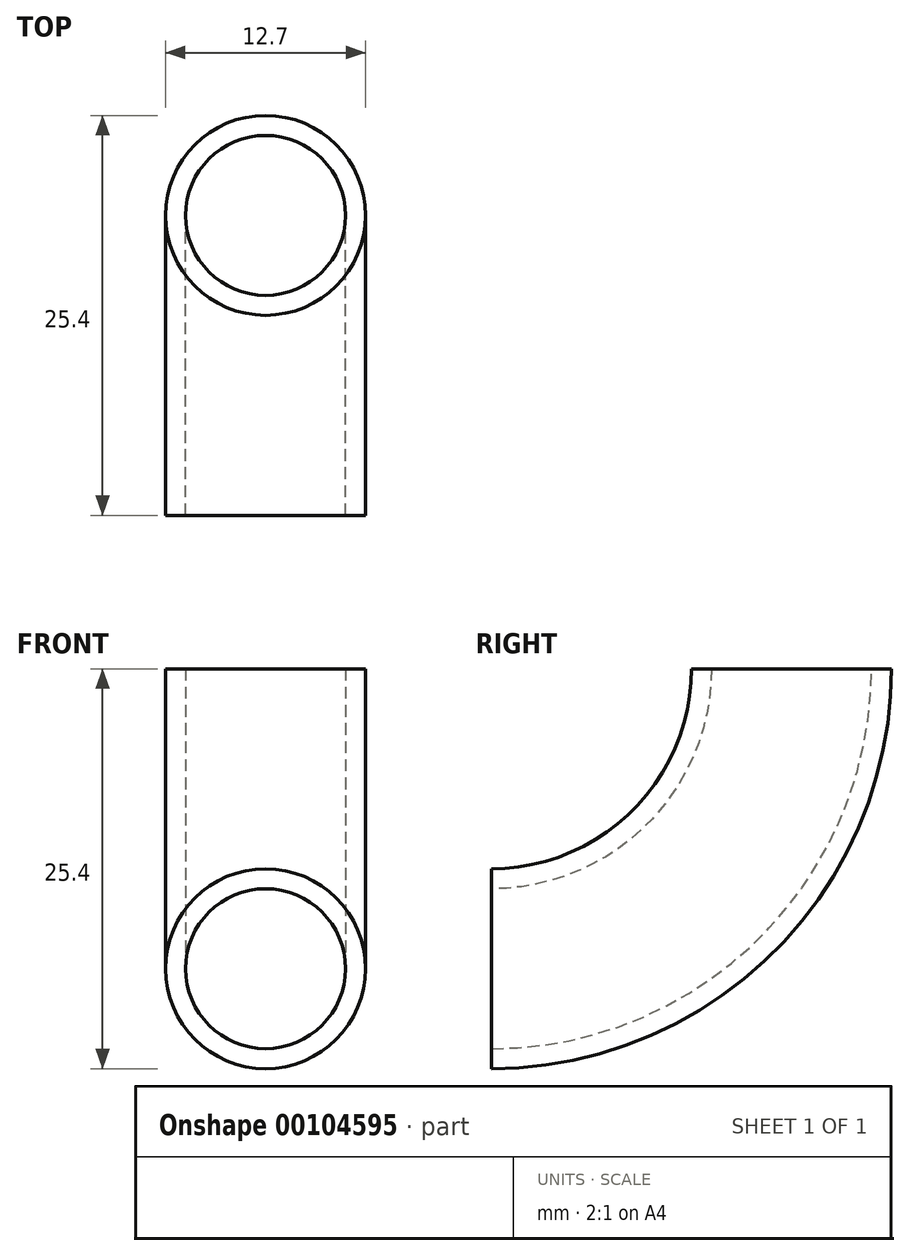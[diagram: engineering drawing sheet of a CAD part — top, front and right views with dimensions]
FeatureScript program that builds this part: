
annotation { "Feature Type Name" : "Feature", "Feature Type Description" : "" }
export const myFeature = defineFeature(function(context is Context, id is Id, definition is map)
    precondition{}
    {
        {
            var Q0;
            Q0=qCreatedBy(makeId("Front.planeOp"),FACE);
            var sketch = newSketch(context, id + "F0", { "sketchPlane" : qUnion([Q0])});
            skCircle(sketch, "E0", {"center": v(0, 0) * mm, "radius": 6.35 * mm});
            skCircle(sketch, "E1", {"center": v(0, 0) * mm, "radius": 5.08 * mm});
            skSolve(sketch);
        }
        {
            var Q0;
            Q0=qCreatedBy(makeId("Right.planeOp"),FACE);
            var sketch = newSketch(context, id + "F1", { "sketchPlane" : qUnion([Q0])});
            skArc(sketch, "E2", {"start": v(0, 0) * mm, "mid": v(13.47, 5.58) * mm, "end": v(19.05, 19.05) * mm});
            skPoint(sketch, "E3.orphan", {"position": v(0, 38.1) * mm});
            skSolve(sketch);
        }
        {
            var Q0;
            Q0=makeQuery(id+"F0.imprint","IMPRINT",FACE,{"disambiguationData":[TD([[makeQuery(id+"F0.imprint","IMPRINT",EDGE,{"derivedFrom":sQuery(id+"F0.wireOp",EDGE,"E0")}),1.0]])]});
            var Q1;
            Q1=sQuery(id+"F1.wireOp",EDGE,"E2");
            sweep(context, id + "F2", {"profiles" : qUnion([Q0]), "path" : qUnion([Q1])});
        }
    });
